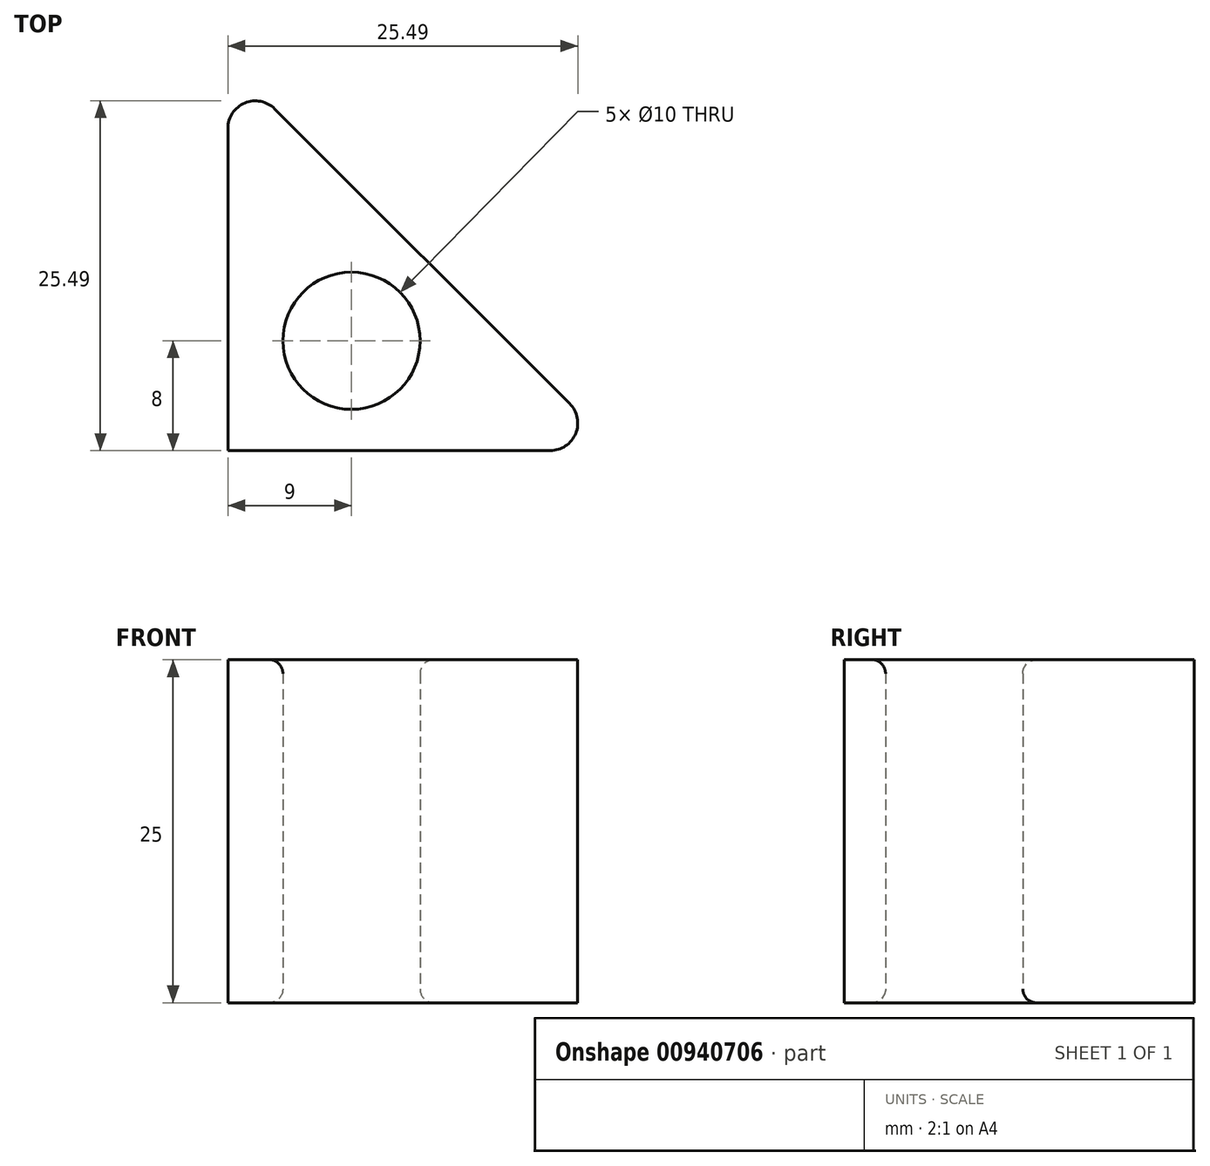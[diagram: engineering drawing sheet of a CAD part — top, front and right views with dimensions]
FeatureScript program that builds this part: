
annotation { "Feature Type Name" : "Feature", "Feature Type Description" : "" }
export const myFeature = defineFeature(function(context is Context, id is Id, definition is map)
    precondition{}
    {
        {
            var Q0;
            Q0=qCreatedBy(makeId("Top.planeOp"),FACE);
            var sketch = newSketch(context, id + "F0", { "sketchPlane" : qUnion([Q0])});
            skLineSegment(sketch, "E0.bottom", {"start": v(0, 0) * mm, "end": v(28.31, 0) * mm});
            skLineSegment(sketch, "E0.left", {"start": v(0, 0) * mm, "end": v(0, 28.31) * mm});
            skLineSegment(sketch, "E0.right", {"start": v(28.31, 0) * mm, "end": v(0, 28.31) * mm});
            skCircle(sketch, "E1", {"center": v(9, 8) * mm, "radius": 5 * mm});
            skSolve(sketch);
        }
        {
            var Q0;
            Q0=makeQuery(id+"F0.imprint","IMPRINT",FACE,{"disambiguationData":[TD([[makeQuery(id+"F0.imprint","IMPRINT",EDGE,{"derivedFrom":sQuery(id+"F0.wireOp",EDGE,"E0.bottom")}),1.0]])]});
            extrude(context, id + "F1", {"entities" : qUnion([Q0]), "depth" : 25 * mm, "offsetDistance" : 25 * mm});
        }
        {
            var Q0;
            Q0=makeQuery(id+"F1.opExtrude","SWEPT_EDGE",EDGE,{"disambiguationData":[OSD([sQuery(id+"F0.wireOp",EDGE,"E0.left"),sQuery(id+"F0.wireOp",EDGE,"E0.right")])]});
            var Q1;
            Q1=makeQuery(id+"F1.opExtrude","SWEPT_EDGE",EDGE,{"disambiguationData":[OSD([sQuery(id+"F0.wireOp",EDGE,"E0.bottom"),sQuery(id+"F0.wireOp",EDGE,"E0.right")])]});
            fillet(context, id + "F2", {"entities" : qUnion([Q0, Q1]), "radius" : 2 * mm, "tangentPropagation" : true, "allowEdgeOverflow" : false});
        }
        {
            var Q0;
            Q0=makeQuery(id+"F1.opExtrude","SWEPT_FACE",FACE,{"disambiguationData":[OSD([sQuery(id+"F0.wireOp",EDGE,"E1")])]});
            fillet(context, id + "F3", {"entities" : qUnion([Q0]), "radius" : 1 * mm, "tangentPropagation" : true, "allowEdgeOverflow" : false});
        }
    });
